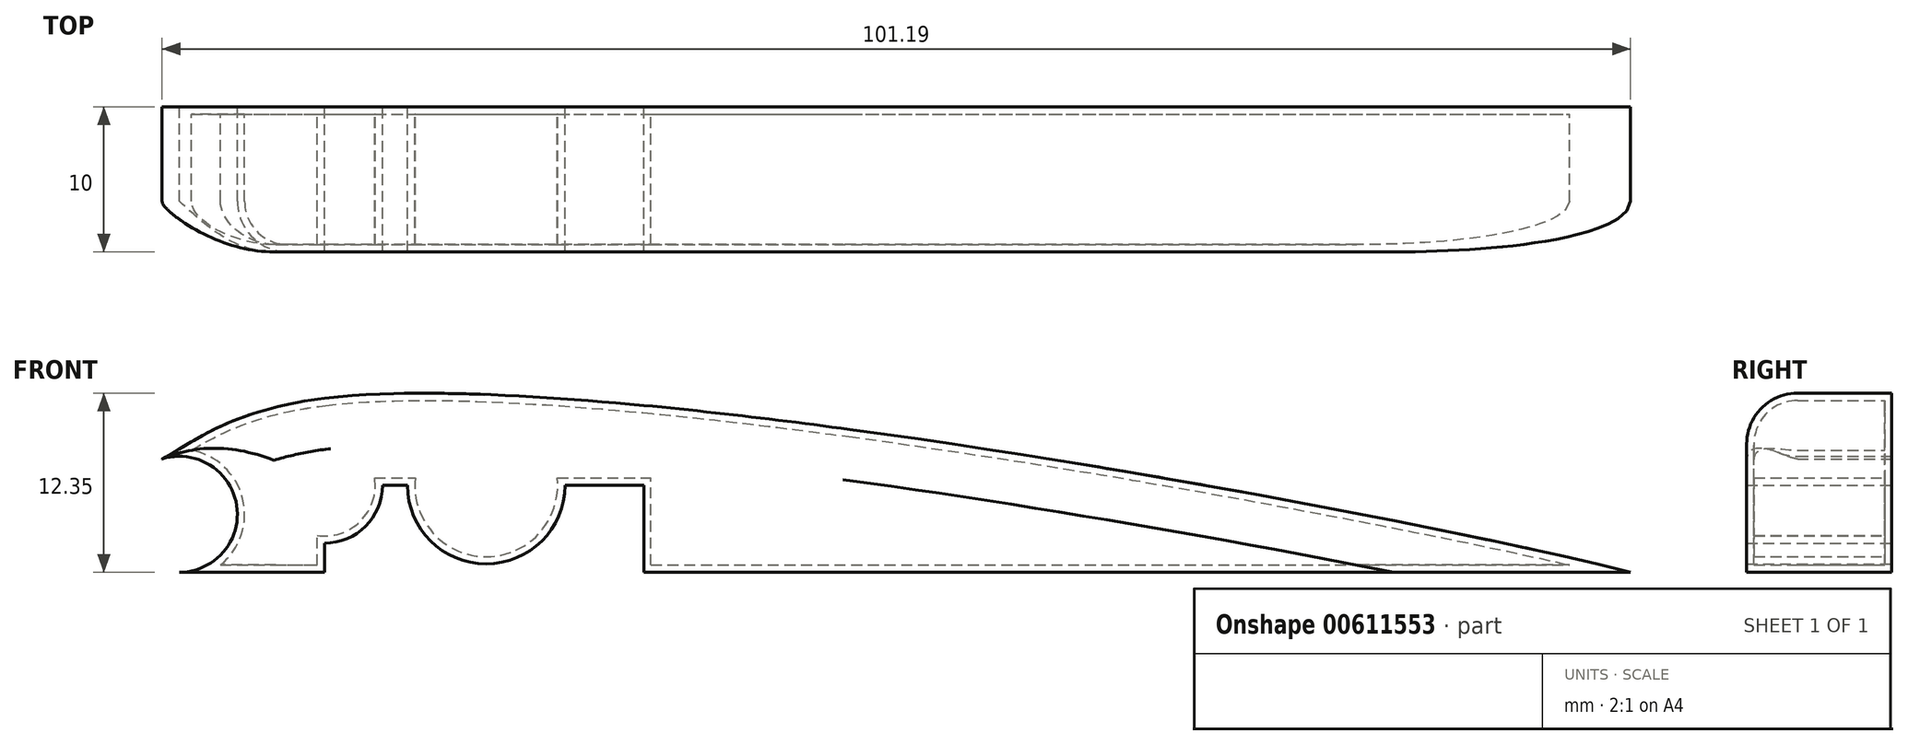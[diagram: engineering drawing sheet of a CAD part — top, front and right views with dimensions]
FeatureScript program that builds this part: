
annotation { "Feature Type Name" : "Feature", "Feature Type Description" : "" }
export const myFeature = defineFeature(function(context is Context, id is Id, definition is map)
    precondition{}
    {
        {
            var Q0;
            Q0=qCreatedBy(makeId("Front.planeOp"),FACE);
            var sketch = newSketch(context, id + "F0", { "sketchPlane" : qUnion([Q0])});
            skLineSegment(sketch, "E0", {"start": v(-54.68, -39.6) * mm, "end": v(-44.68, -39.6) * mm});
            skLineSegment(sketch, "E1", {"start": v(-44.68, -39.6) * mm, "end": v(-19.08, -39.6) * mm});
            skLineSegment(sketch, "E2", {"start": v(-54.68, -39.6) * mm, "end": v(-54.68, -31.6) * mm});
            skLineSegment(sketch, "E3", {"start": v(-44.68, -39.6) * mm, "end": v(-44.68, -27.6) * mm});
            skLineSegment(sketch, "E4", {"start": v(-54.68, -39.6) * mm, "end": v(-54.68, -35.6) * mm});
            skArc(sketch, "E5", {"start": v(-54.68, -39.6) * mm, "mid": v(-58.54, -36.64) * mm, "end": v(-56.7, -32.14) * mm});
            skFitSpline(sketch, "E6", {"points": [v(-56.7, -32.14) * mm, v(-44.68, -27.6) * mm, v(45.32, -39.6) * mm], "startDerivative": vector(25.72, 9) * mm, "endDerivative": vector(55.93, -14.48) * mm});
            skLineSegment(sketch, "E7", {"start": v(-19.08, -39.6) * mm, "end": v(45.32, -39.6) * mm});
            skLineSegment(sketch, "E8", {"start": v(-19.08, -39.6) * mm, "end": v(-22.68, -39.6) * mm});
            skLineSegment(sketch, "E9", {"start": v(-22.68, -39.6) * mm, "end": v(-22.68, -28.1) * mm});
            skCircle(sketch, "E10", {"center": v(-54.68, -35.6) * mm, "radius": 4 * mm});
            skLineSegment(sketch, "E11", {"start": v(-44.68, -39.6) * mm, "end": v(-44.68, -33.6) * mm});
            skCircle(sketch, "E12", {"center": v(-44.68, -33.6) * mm, "radius": 4 * mm});
            skLineSegment(sketch, "E13.right", {"start": v(-8.48, -24.79) * mm, "end": v(-8.48, -41.72) * mm});
            skLineSegment(sketch, "E14", {"start": v(-44.68, -33.6) * mm, "end": v(-33.53, -33.6) * mm});
            skLineSegment(sketch, "E15", {"start": v(-33.53, -33.6) * mm, "end": v(-22.68, -33.6) * mm});
            skLineSegment(sketch, "E16", {"start": v(-22.68, -33.6) * mm, "end": v(-8.48, -34.63) * mm});
            skCircle(sketch, "E17", {"center": v(-33.53, -33.6) * mm, "radius": 5.42 * mm});
            skCircle(sketch, "E18", {"center": v(-8.48, -34.63) * mm, "radius": 4.1 * mm});
            skLineSegment(sketch, "E19", {"start": v(-54.68, -35.6) * mm, "end": v(-54.68, -18.88) * mm});
            skLineSegment(sketch, "E20", {"start": v(-54.68, -18.88) * mm, "end": v(-23.08, -18.88) * mm});
            skLineSegment(sketch, "E21", {"start": v(-54.68, -18.88) * mm, "end": v(-54.68, -4.66) * mm});
            skLineSegment(sketch, "E22", {"start": v(-54.68, -4.66) * mm, "end": v(-20.24, -4.66) * mm});
            skLineSegment(sketch, "E23", {"start": v(-54.68, -4.66) * mm, "end": v(-54.68, 32.52) * mm});
            skPoint(sketch, "E23.endSnap0", {"position": v(-54.68, -11.77) * mm});
            skLineSegment(sketch, "E24", {"start": v(-54.68, 32.52) * mm, "end": v(-33.72, 32.52) * mm});
            skLineSegment(sketch, "E25", {"start": v(-54.68, -39.6) * mm, "end": v(-62.97, -39.6) * mm});
            skLineSegment(sketch, "E26", {"start": v(-8.48, -29.75) * mm, "end": v(-8.48, -39.6) * mm});
            skSolve(sketch);
        }
        {
            var Q0;
            {var subQ1=sQuery(id+"F0.wireOp",EDGE,"E3");var subQ10=sQuery(id+"F0.wireOp",EDGE,"E6");var subQ12=makeQuery(id+"F0.imprint","INTERSECT",VERTEX,{"derivedFrom":[subQ1,subQ10]});Q0=makeQuery(id+"F0.imprint","IMPRINT",FACE,{"disambiguationData":[TD([[makeQuery(id+"F0.imprint","IMPRINT",EDGE,{"disambiguationData":[TD([[subQ12,1.0]])],"derivedFrom":subQ1}),-1.0]])]});}
            var Q1;
            {var subQ1=sQuery(id+"F0.wireOp",EDGE,"E1");Q1=makeQuery(id+"F0.imprint","IMPRINT",FACE,{"disambiguationData":[TD([[makeQuery(id+"F0.imprint","IMPRINT",EDGE,{"derivedFrom":subQ1}),1.0]])]});}
            var Q2;
            {var subQ1=sQuery(id+"F0.wireOp",EDGE,"E0");Q2=makeQuery(id+"F0.imprint","IMPRINT",FACE,{"disambiguationData":[TD([[makeQuery(id+"F0.imprint","IMPRINT",EDGE,{"derivedFrom":subQ1}),1.0]])]});}
            var Q3;
            {var subQ0=sQuery(id+"F0.wireOp",EDGE,"E4");Q3=makeQuery(id+"F0.imprint","IMPRINT",FACE,{"disambiguationData":[TD([[makeQuery(id+"F0.imprint","IMPRINT",EDGE,{"derivedFrom":subQ0}),-1.0]])]});}
            var Q4;
            {var subQ1=sQuery(id+"F0.wireOp",EDGE,"E4");Q4=makeQuery(id+"F0.imprint","IMPRINT",FACE,{"disambiguationData":[TD([[makeQuery(id+"F0.imprint","IMPRINT",EDGE,{"derivedFrom":subQ1}),1.0]])]});}
            var Q5;
            {var subQ1=sQuery(id+"F0.wireOp",EDGE,"E8");Q5=makeQuery(id+"F0.imprint","IMPRINT",FACE,{"disambiguationData":[TD([[makeQuery(id+"F0.imprint","IMPRINT",EDGE,{"derivedFrom":subQ1}),-1.0]])]});}
            var Q6;
            {var subQ1=sQuery(id+"F0.wireOp",EDGE,"E6");var subQ5=sQuery(id+"F0.wireOp",EDGE,"E9");var subQ6=makeQuery(id+"F0.imprint","INTERSECT",VERTEX,{"derivedFrom":[subQ1,subQ5]});Q6=makeQuery(id+"F0.imprint","IMPRINT",FACE,{"disambiguationData":[TD([[makeQuery(id+"F0.imprint","IMPRINT",EDGE,{"disambiguationData":[TD([[subQ6,-1.0]])],"derivedFrom":subQ1}),-1.0]])]});}
            var Q7;
            {var subQ1=sQuery(id+"F0.wireOp",EDGE,"E7");var subQ5=sQuery(id+"F0.wireOp",EDGE,"E6");var subQ6=makeQuery(id+"F0.imprint","INTERSECT",VERTEX,{"derivedFrom":[subQ5,subQ1]});Q7=makeQuery(id+"F0.imprint","IMPRINT",FACE,{"disambiguationData":[TD([[makeQuery(id+"F0.imprint","IMPRINT",EDGE,{"disambiguationData":[TD([[subQ6,1.0]])],"derivedFrom":subQ5}),-1.0]])]});}
            var Q8;
            {var subQ0=sQuery(id+"F0.wireOp",EDGE,"E19");var subQ1=sQuery(id+"F0.wireOp",EDGE,"E6");var subQ2=makeQuery(id+"F0.imprint","INTERSECT",VERTEX,{"derivedFrom":[subQ1,subQ0]});Q8=makeQuery(id+"F0.imprint","IMPRINT",FACE,{"disambiguationData":[TD([[makeQuery(id+"F0.imprint","IMPRINT",EDGE,{"disambiguationData":[TD([[subQ2,1.0]])],"derivedFrom":subQ1}),-1.0]])]});}
            var Q9;
            {var subQ0=sQuery(id+"F0.wireOp",EDGE,"E15");var subQ1=sQuery(id+"F0.wireOp",EDGE,"E14");var subQ2=makeQuery(id+"F0.imprint","INTERSECT",VERTEX,{"derivedFrom":[subQ1,subQ0]});Q9=makeQuery(id+"F0.imprint","IMPRINT",FACE,{"disambiguationData":[TD([[makeQuery(id+"F0.imprint","IMPRINT",EDGE,{"disambiguationData":[TD([[subQ2,1.0]])],"derivedFrom":subQ1}),-1.0]])]});}
            var Q10;
            {var subQ0=sQuery(id+"F0.wireOp",EDGE,"E15");var subQ1=sQuery(id+"F0.wireOp",EDGE,"E14");var subQ2=makeQuery(id+"F0.imprint","INTERSECT",VERTEX,{"derivedFrom":[subQ1,subQ0]});Q10=makeQuery(id+"F0.imprint","IMPRINT",FACE,{"disambiguationData":[TD([[makeQuery(id+"F0.imprint","IMPRINT",EDGE,{"disambiguationData":[TD([[subQ2,1.0]])],"derivedFrom":subQ1}),1.0]])]});}
            var Q11;
            {var subQ1=sQuery(id+"F0.wireOp",EDGE,"E11");var subQ3=sQuery(id+"F0.wireOp",EDGE,"E12");var subQ4=makeQuery(id+"F0.imprint","INTERSECT",VERTEX,{"derivedFrom":[subQ1,subQ3]});Q11=makeQuery(id+"F0.imprint","IMPRINT",FACE,{"disambiguationData":[TD([[makeQuery(id+"F0.imprint","IMPRINT",EDGE,{"disambiguationData":[TD([[subQ4,-1.0]])],"derivedFrom":subQ3}),1.0]])]});}
            var Q12;
            {var subQ1=sQuery(id+"F0.wireOp",EDGE,"E3");var subQ3=sQuery(id+"F0.wireOp",EDGE,"E12");var subQ4=makeQuery(id+"F0.imprint","INTERSECT",VERTEX,{"derivedFrom":[subQ1,subQ3]});Q12=makeQuery(id+"F0.imprint","IMPRINT",FACE,{"disambiguationData":[TD([[makeQuery(id+"F0.imprint","IMPRINT",EDGE,{"disambiguationData":[TD([[subQ4,1.0]])],"derivedFrom":subQ3}),1.0]])]});}
            var Q13;
            {var subQ1=sQuery(id+"F0.wireOp",EDGE,"E3");var subQ3=sQuery(id+"F0.wireOp",EDGE,"E12");var subQ4=makeQuery(id+"F0.imprint","INTERSECT",VERTEX,{"derivedFrom":[subQ1,subQ3]});Q13=makeQuery(id+"F0.imprint","IMPRINT",FACE,{"disambiguationData":[TD([[makeQuery(id+"F0.imprint","IMPRINT",EDGE,{"disambiguationData":[TD([[subQ4,-1.0]])],"derivedFrom":subQ3}),1.0]])]});}
            var Q14;
            {var subQ0=sQuery(id+"F0.wireOp",EDGE,"E13.right");var subQ1=makeQuery(id+"F0.imprint","INTERSECT",VERTEX,{"derivedFrom":[subQ0,sQuery(id+"F0.wireOp",EDGE,"E16")]});Q14=makeQuery(id+"F0.imprint","IMPRINT",FACE,{"disambiguationData":[TD([[makeQuery(id+"F0.imprint","IMPRINT",EDGE,{"disambiguationData":[TD([[subQ1,1.0]])],"derivedFrom":subQ0}),1.0]])]});}
            var Q15;
            {var subQ0=sQuery(id+"F0.wireOp",EDGE,"E16");var subQ1=sQuery(id+"F0.wireOp",EDGE,"E13.right");var subQ2=makeQuery(id+"F0.imprint","INTERSECT",VERTEX,{"derivedFrom":[subQ1,subQ0]});Q15=makeQuery(id+"F0.imprint","IMPRINT",FACE,{"disambiguationData":[TD([[makeQuery(id+"F0.imprint","IMPRINT",EDGE,{"disambiguationData":[TD([[subQ2,1.0]])],"derivedFrom":subQ1}),-1.0]])]});}
            var Q16;
            {var subQ0=sQuery(id+"F0.wireOp",EDGE,"E16");var subQ1=sQuery(id+"F0.wireOp",EDGE,"E13.right");var subQ2=makeQuery(id+"F0.imprint","INTERSECT",VERTEX,{"derivedFrom":[subQ1,subQ0]});Q16=makeQuery(id+"F0.imprint","IMPRINT",FACE,{"disambiguationData":[TD([[makeQuery(id+"F0.imprint","IMPRINT",EDGE,{"disambiguationData":[TD([[subQ2,-1.0]])],"derivedFrom":subQ1}),-1.0]])]});}
            var Q17;
            {var subQ0=sQuery(id+"F0.wireOp",EDGE,"E26");var subQ1=sQuery(id+"F0.wireOp",EDGE,"E18");var subQ2=makeQuery(id+"F0.imprint","INTERSECT",VERTEX,{"disambiguationData":[OD(0.0)],"derivedFrom":[subQ1,subQ0]});Q17=makeQuery(id+"F0.imprint","IMPRINT",FACE,{"disambiguationData":[TD([[makeQuery(id+"F0.imprint","IMPRINT",EDGE,{"disambiguationData":[TD([[subQ2,1.0]])],"derivedFrom":subQ1}),1.0]])]});}
            var Q18;
            {var subQ0=sQuery(id+"F0.wireOp",EDGE,"E26");var subQ1=sQuery(id+"F0.wireOp",EDGE,"E16");var subQ2=makeQuery(id+"F0.imprint","INTERSECT",VERTEX,{"derivedFrom":[subQ1,subQ0]});Q18=makeQuery(id+"F0.imprint","IMPRINT",FACE,{"disambiguationData":[TD([[makeQuery(id+"F0.imprint","IMPRINT",EDGE,{"disambiguationData":[TD([[subQ2,1.0]])],"derivedFrom":subQ1}),1.0]])]});}
            var Q19;
            {var subQ0=sQuery(id+"F0.wireOp",EDGE,"E26");var subQ1=sQuery(id+"F0.wireOp",EDGE,"E16");var subQ2=makeQuery(id+"F0.imprint","INTERSECT",VERTEX,{"derivedFrom":[subQ1,subQ0]});Q19=makeQuery(id+"F0.imprint","IMPRINT",FACE,{"disambiguationData":[TD([[makeQuery(id+"F0.imprint","IMPRINT",EDGE,{"disambiguationData":[TD([[subQ2,1.0]])],"derivedFrom":subQ1}),-1.0]])]});}
            extrude(context, id + "F1", {"entities" : qUnion([Q0, Q1, Q2, Q3, Q4, Q5, Q6, Q7, Q8, Q9, Q10, Q11, Q12, Q13, Q14, Q15, Q16, Q17, Q18, Q19]), "depth" : 10 * mm, "offsetDistance" : 25 * mm});
        }
        {
            var Q0;
            Q0=makeQuery(id+"F1.opExtrude","CAP_EDGE",EDGE,{"disambiguationData":[OSD([sQuery(id+"F0.wireOp",EDGE,"E6")])],"isStart":false});
            var Q1;
            Q1=makeQuery(id+"F1.opExtrude","CAP_EDGE",EDGE,{"disambiguationData":[OSD([sQuery(id+"F0.wireOp",EDGE,"E10")])],"isStart":false});
            fillet(context, id + "F2", {"entities" : qUnion([Q0, Q1]), "radius" : 3.5 * mm, "tangentPropagation" : true, "allowEdgeOverflow" : false});
        }
        {
            var Q0;
            Q0=makeQuery(id+"F1.opExtrude","CAP_FACE",FACE,{"disambiguationData":[OSD([sQuery(id+"F0.wireOp",EDGE,"E0"),sQuery(id+"F0.wireOp",EDGE,"E1"),sQuery(id+"F0.wireOp",EDGE,"E6"),sQuery(id+"F0.wireOp",EDGE,"E7"),sQuery(id+"F0.wireOp",EDGE,"E8"),sQuery(id+"F0.wireOp",EDGE,"E10")])],"isStart":true});
            var Q1;
            Q1=makeQuery(id+"F1.opExtrude","SWEPT_BODY",BODY,{"disambiguationData":[OSD([sQuery(id+"F0.wireOp",EDGE,"E0"),sQuery(id+"F0.wireOp",EDGE,"E1"),sQuery(id+"F0.wireOp",EDGE,"E6"),sQuery(id+"F0.wireOp",EDGE,"E7"),sQuery(id+"F0.wireOp",EDGE,"E8"),sQuery(id+"F0.wireOp",EDGE,"E10")])]});
            shell(context, id + "F3", {"isHollow" : true, "entities" : qUnion([Q0]), "parts" : qUnion([Q1]), "thickness" : 0.5 * mm});
        }
    });
